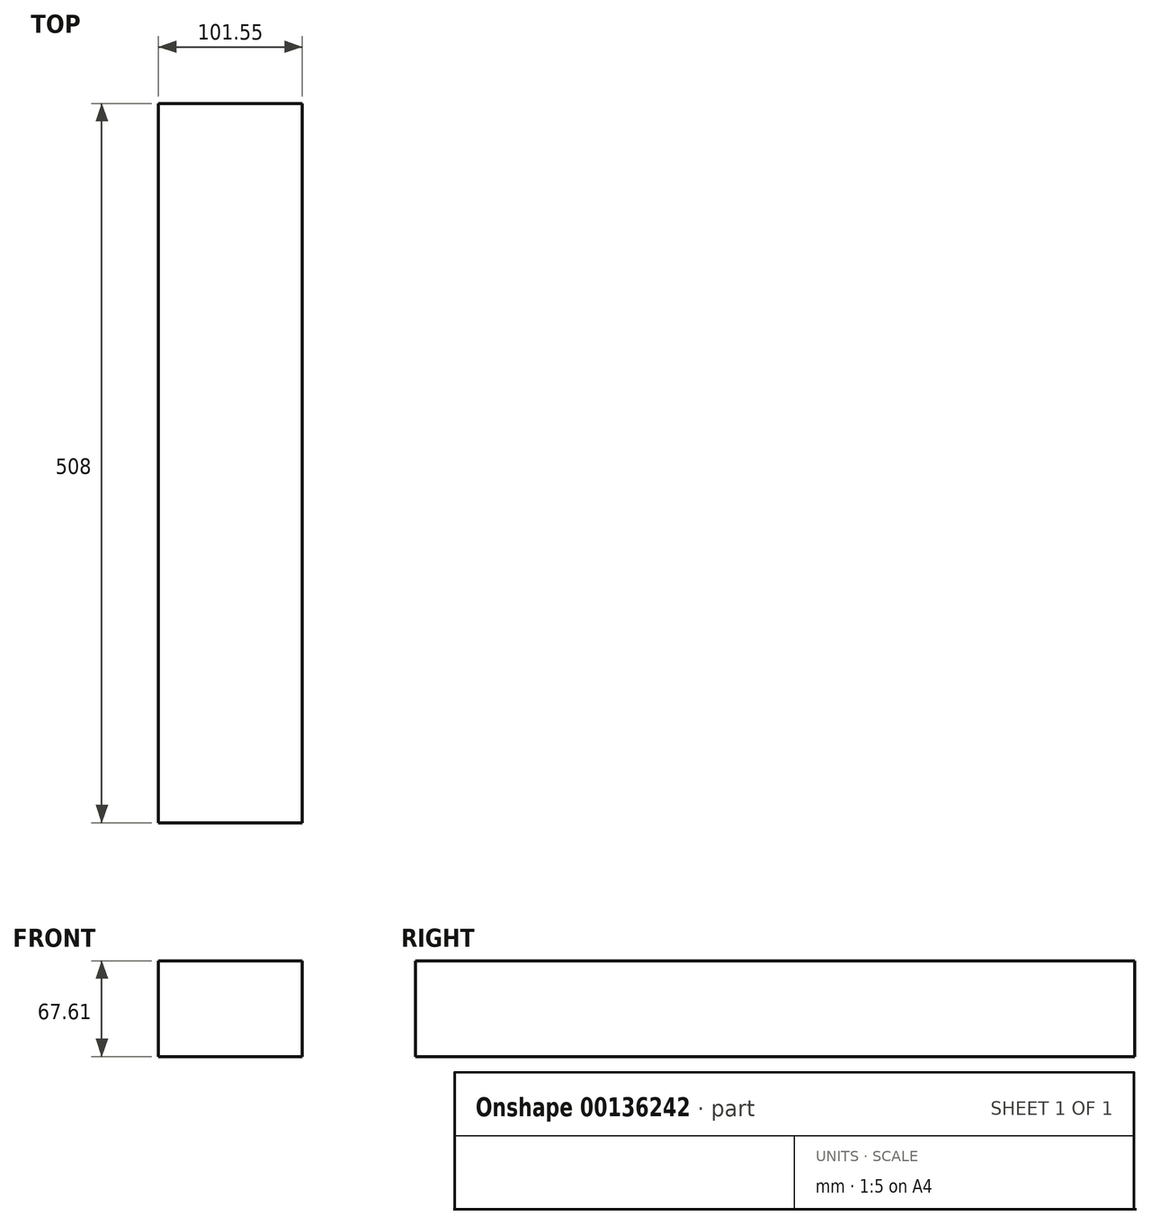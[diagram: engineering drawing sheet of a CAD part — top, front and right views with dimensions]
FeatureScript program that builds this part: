
annotation { "Feature Type Name" : "Feature", "Feature Type Description" : "" }
export const myFeature = defineFeature(function(context is Context, id is Id, definition is map)
    precondition{}
    {
        {
            var Q0;
            Q0=qCreatedBy(makeId("Front.planeOp"),FACE);
            var sketch = newSketch(context, id + "F0", { "sketchPlane" : qUnion([Q0])});
            skLineSegment(sketch, "E0", {"start": v(-49.92, 38.94) * mm, "end": v(51.63, 38.94) * mm});
            skLineSegment(sketch, "E1", {"start": v(51.63, 38.94) * mm, "end": v(51.63, -28.67) * mm});
            skLineSegment(sketch, "E2", {"start": v(51.63, -28.67) * mm, "end": v(-49.92, -28.67) * mm});
            skLineSegment(sketch, "E3", {"start": v(-49.92, -28.67) * mm, "end": v(-49.92, 38.94) * mm});
            skSolve(sketch);
        }
        {
            var Q0;
            Q0=makeQuery(id+"F0.imprint","IMPRINT",FACE,{"disambiguationData":[TD([[makeQuery(id+"F0.imprint","IMPRINT",EDGE,{"derivedFrom":sQuery(id+"F0.wireOp",EDGE,"E0")}),-1.0]])]});
            extrude(context, id + "F1", {"entities" : qUnion([Q0]), "depth" : 508 * mm});
        }
    });
